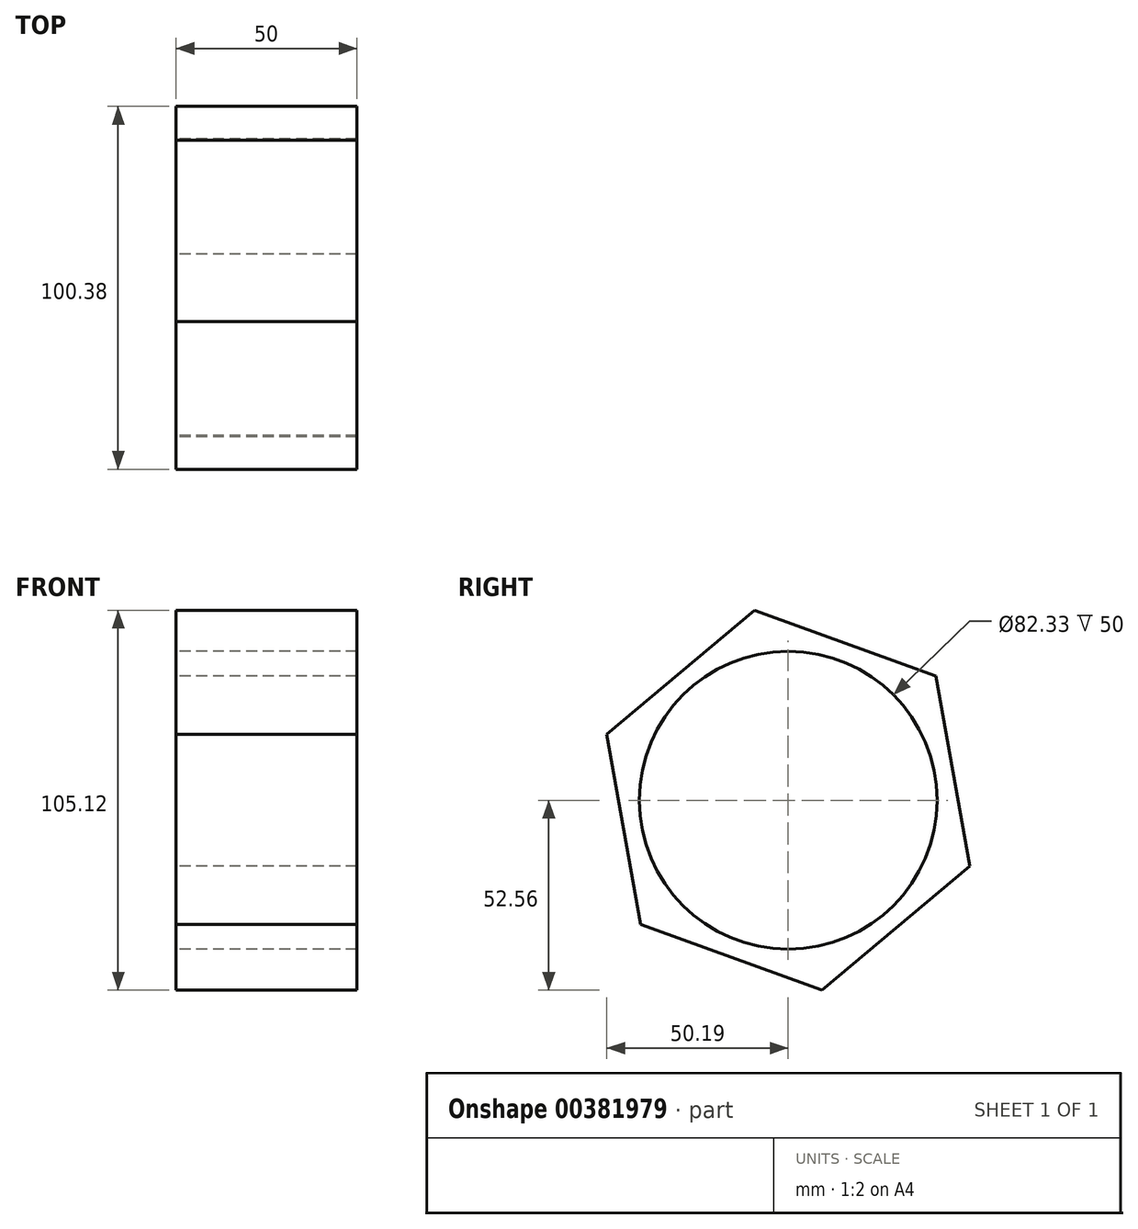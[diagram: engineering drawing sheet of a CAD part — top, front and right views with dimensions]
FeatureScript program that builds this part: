
annotation { "Feature Type Name" : "Feature", "Feature Type Description" : "" }
export const myFeature = defineFeature(function(context is Context, id is Id, definition is map)
    precondition{}
    {
        {
            var Q0;
            Q0=qCreatedBy(makeId("Right.planeOp"),FACE);
            var sketch = newSketch(context, id + "F0", { "sketchPlane" : qUnion([Q0])});
            skCircle(sketch, "E0.cCircle", {"center": v(0, 0) * mm, "radius": 46.23 * mm, "construction": true});
            skLineSegment(sketch, "E0.0", {"start": v(-50.19, 18.2) * mm, "end": v(-9.33, 52.56) * mm});
            skLineSegment(sketch, "E0.1", {"start": v(-9.33, 52.56) * mm, "end": v(40.86, 34.36) * mm});
            skLineSegment(sketch, "E0.2", {"start": v(40.86, 34.36) * mm, "end": v(50.19, -18.2) * mm});
            skLineSegment(sketch, "E0.3", {"start": v(50.19, -18.2) * mm, "end": v(9.33, -52.56) * mm});
            skLineSegment(sketch, "E0.4", {"start": v(9.33, -52.56) * mm, "end": v(-40.86, -34.36) * mm});
            skLineSegment(sketch, "E0.5", {"start": v(-40.86, -34.36) * mm, "end": v(-50.19, 18.2) * mm});
            skPoint(sketch, "E0.0.midPoint", {"position": v(-29.76, 35.38) * mm});
            skSolve(sketch);
        }
        {
            var Q0;
            Q0 = qSketchRegion(id + "F0", true);
            extrude(context, id + "F1", {"entities" : qUnion([Q0]), "depth" : 50 * mm});
        }
        {
            var Q0;
            Q0=qCreatedBy(makeId("Right.planeOp"),FACE);
            var sketch = newSketch(context, id + "F2", { "sketchPlane" : qUnion([Q0])});
            skCircle(sketch, "E1", {"center": v(0, 0) * mm, "radius": 41.17 * mm});
            skSolve(sketch);
        }
        {
            var Q0;
            Q0 = qSketchRegion(id + "F2", true);
            extrude(context, id + "F3", {"entities" : qUnion([Q0]), "operationType" : NewBodyOperationType.REMOVE, "endBound" : BoundingType.THROUGH_ALL, "depth" : 25 * mm});
        }
    });
